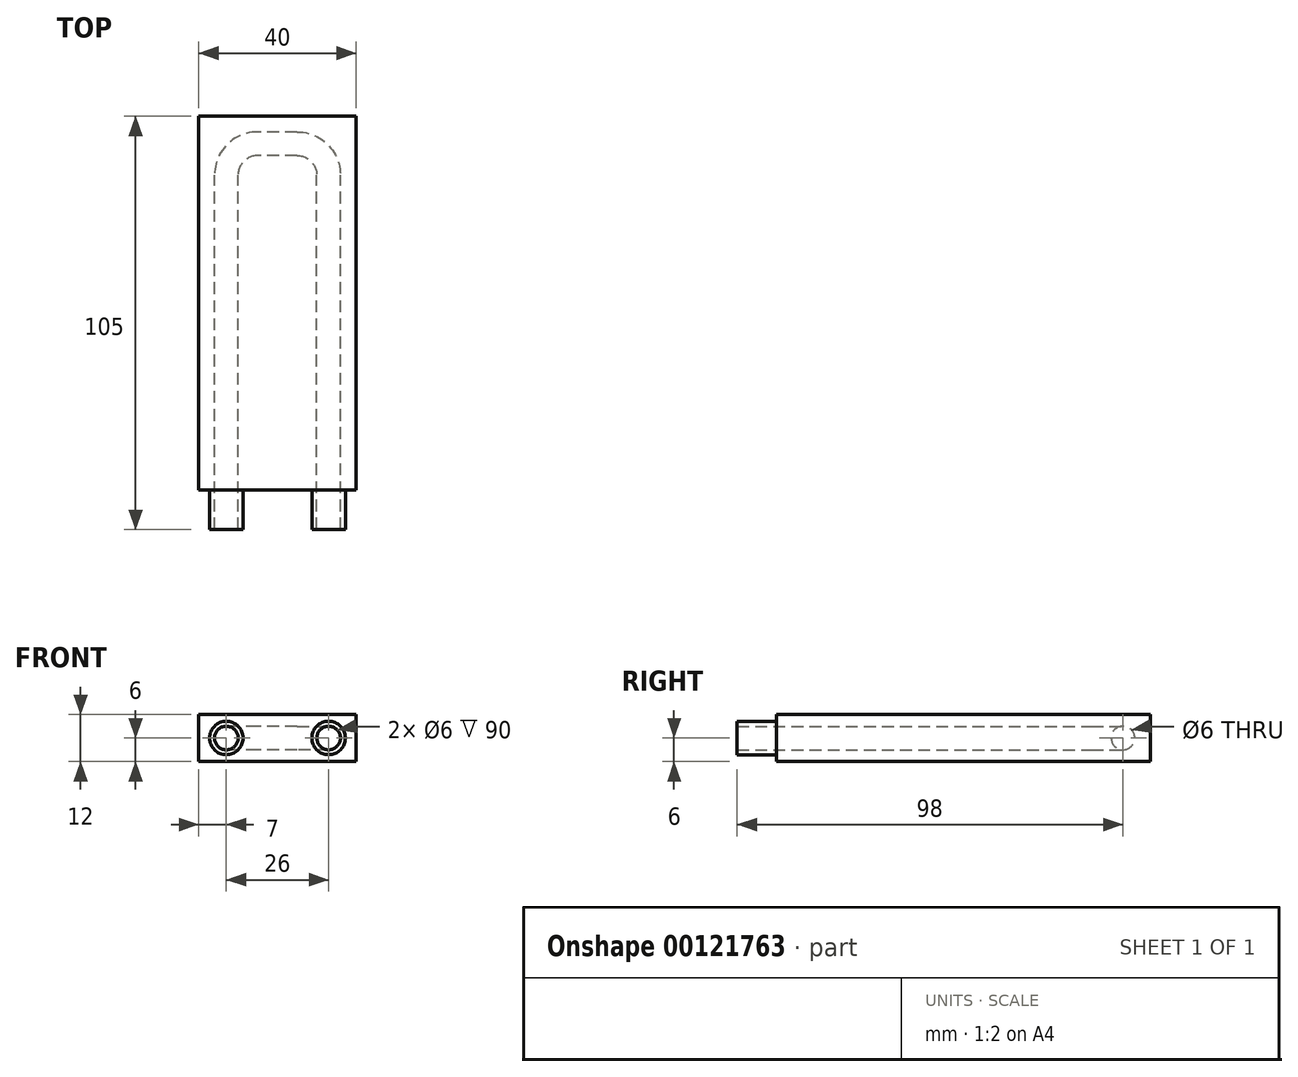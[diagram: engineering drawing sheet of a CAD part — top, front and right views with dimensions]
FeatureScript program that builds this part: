
annotation { "Feature Type Name" : "Feature", "Feature Type Description" : "" }
export const myFeature = defineFeature(function(context is Context, id is Id, definition is map)
    precondition{}
    {
        {
            var Q0;
            Q0=qCreatedBy(makeId("Top.planeOp"),FACE);
            var sketch = newSketch(context, id + "F0", { "sketchPlane" : qUnion([Q0])});
            skLineSegment(sketch, "E0.bottom", {"start": v(0, 0) * mm, "end": v(20, 0) * mm});
            skLineSegment(sketch, "E0.top", {"start": v(0, 95) * mm, "end": v(20, 95) * mm});
            skLineSegment(sketch, "E0.left", {"start": v(0, 0) * mm, "end": v(0, 95) * mm});
            skLineSegment(sketch, "E0.right", {"start": v(20, 0) * mm, "end": v(20, 95) * mm});
            skPoint(sketch, "E1.MirrorCS.end.orphan", {"position": v(-20, 95) * mm});
            skPoint(sketch, "E1.MirrorCS.start.orphan", {"position": v(0, 95) * mm});
            skPoint(sketch, "E2.MirrorCS.end.orphan", {"position": v(-20, 0) * mm});
            skPoint(sketch, "E2.MirrorCS.start.orphan", {"position": v(0, 0) * mm});
            skSolve(sketch);
        }
        {
            var Q0;
            Q0 = qSketchRegion(id + "F0", true);
            extrude(context, id + "F1", {"entities" : qUnion([Q0]), "endBound" : BoundingType.SYMMETRIC, "depth" : 12 * mm});
        }
        {
            var Q0;
            Q0=qCreatedBy(makeId("Top.planeOp"),FACE);
            var sketch = newSketch(context, id + "F2", { "sketchPlane" : qUnion([Q0])});
            skLineSegment(sketch, "E3", {"start": v(13, 0) * mm, "end": v(13, 80) * mm});
            skLineSegment(sketch, "E4", {"start": v(5, 88) * mm, "end": v(0, 88) * mm});
            skPoint(sketch, "E5.visualSharp", {"position": v(13, 88) * mm});
            skArc(sketch, "E5.filletArc", {"start": v(13, 80) * mm, "mid": v(10.66, 85.66) * mm, "end": v(5, 88) * mm});
            skSolve(sketch);
        }
        {
            var Q0;
            Q0=makeQuery(id+"F1.opExtrude","SWEPT_FACE",FACE,{"disambiguationData":[OSD([sQuery(id+"F0.wireOp",EDGE,"E0.bottom")])]});
            var sketch = newSketch(context, id + "F3", { "sketchPlane" : qUnion([Q0])});
            skCircle(sketch, "E6", {"center": v(13, 0) * mm, "radius": 3 * mm});
            skPoint(sketch, "E6.centerSnap0", {"position": v(20, 0) * mm});
            skSolve(sketch);
        }
        {
            var Q0;
            Q0 = qSketchRegion(id + "F3", true);
            var Q1;
            Q1 = qConstructionFilter(qBodyType(qCreatedBy(id + "F2" ,EDGE), BodyType.WIRE), ConstructionObject.NO);
            sweep(context, id + "F4", {"operationType" : NewBodyOperationType.REMOVE, "profiles" : qUnion([Q0]), "path" : qUnion([Q1])});
        }
        {
            var Q0;
            Q0=makeQuery(id+"F1.opExtrude","SWEPT_FACE",FACE,{"disambiguationData":[OSD([sQuery(id+"F0.wireOp",EDGE,"E0.bottom")])]});
            var sketch = newSketch(context, id + "F5", { "sketchPlane" : qUnion([Q0])});
            skCircle(sketch, "E7.0", {"center": v(13, 0) * mm, "radius": 3 * mm});
            skCircle(sketch, "E8", {"center": v(13, 0) * mm, "radius": 4.25 * mm});
            skSolve(sketch);
        }
        {
            var Q0;
            Q0 = qSketchRegion(id + "F5", true);
            extrude(context, id + "F6", {"entities" : qUnion([Q0]), "operationType" : NewBodyOperationType.ADD, "depth" : 10 * mm});
        }
        {
            var Q0;
            Q0=makeQuery(id+"F1.opExtrude","SWEPT_BODY",BODY,{"disambiguationData":[OSD([sQuery(id+"F0.wireOp",EDGE,"E0.bottom"),sQuery(id+"F0.wireOp",EDGE,"E0.top"),sQuery(id+"F0.wireOp",EDGE,"E0.left"),sQuery(id+"F0.wireOp",EDGE,"E0.right")])]});
            var Q1;
            Q1=makeQuery(id+"F6.opExtrude","SWEPT_BODY",BODY,{"disambiguationData":[OSD([sQuery(id+"F5.wireOp",EDGE,"E7.0"),sQuery(id+"F5.wireOp",EDGE,"E8")])]});
            var Q2;
            Q2=makeQuery(id+"F1.opExtrude","SWEPT_FACE",FACE,{"disambiguationData":[OSD([sQuery(id+"F0.wireOp",EDGE,"E0.left")])]});
            mirror(context, id + "F7", {"operationType" : NewBodyOperationType.ADD, "entities" : qUnion([Q0, Q1]), "mirrorPlane" : qUnion([Q2])});
        }
    });
